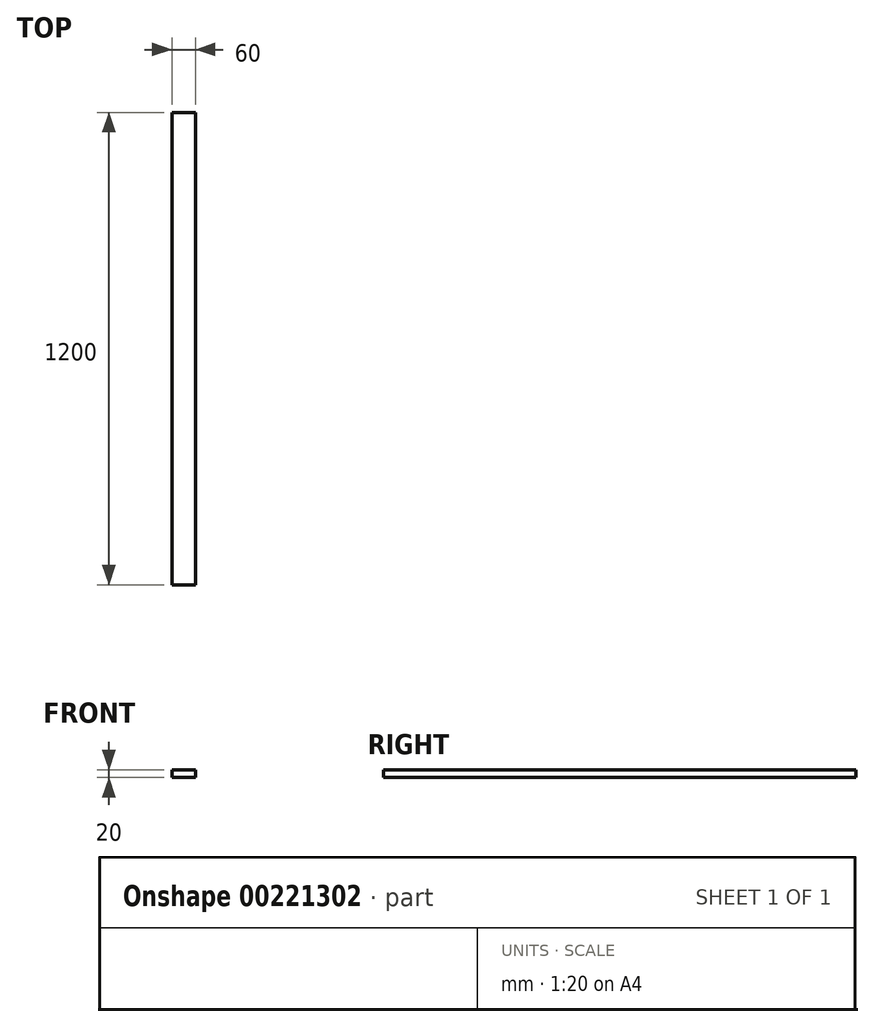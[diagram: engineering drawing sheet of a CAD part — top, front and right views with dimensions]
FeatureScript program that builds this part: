
annotation { "Feature Type Name" : "Feature", "Feature Type Description" : "" }
export const myFeature = defineFeature(function(context is Context, id is Id, definition is map)
    precondition{}
    {
        {
            var Q0;
            Q0=qCreatedBy(makeId("Front.planeOp"),FACE);
            var sketch = newSketch(context, id + "F0", { "sketchPlane" : qUnion([Q0])});
            skLineSegment(sketch, "E0.bottom", {"start": v(-21.52, 12.77) * mm, "end": v(38.48, 12.77) * mm});
            skLineSegment(sketch, "E0.top", {"start": v(-21.52, -7.23) * mm, "end": v(38.48, -7.23) * mm});
            skLineSegment(sketch, "E0.left", {"start": v(-21.52, 12.77) * mm, "end": v(-21.52, -7.23) * mm});
            skLineSegment(sketch, "E0.right", {"start": v(38.48, 12.77) * mm, "end": v(38.48, -7.23) * mm});
            skSolve(sketch);
        }
        {
            var Q0;
            Q0=makeQuery(id+"F0.imprint","IMPRINT",FACE,{"disambiguationData":[TD([[makeQuery(id+"F0.imprint","IMPRINT",EDGE,{"derivedFrom":sQuery(id+"F0.wireOp",EDGE,"E0.bottom")}),-1.0]])]});
            extrude(context, id + "F1", {"entities" : qUnion([Q0]), "oppositeDirection" : true, "depth" : 1200 * mm});
        }
    });
